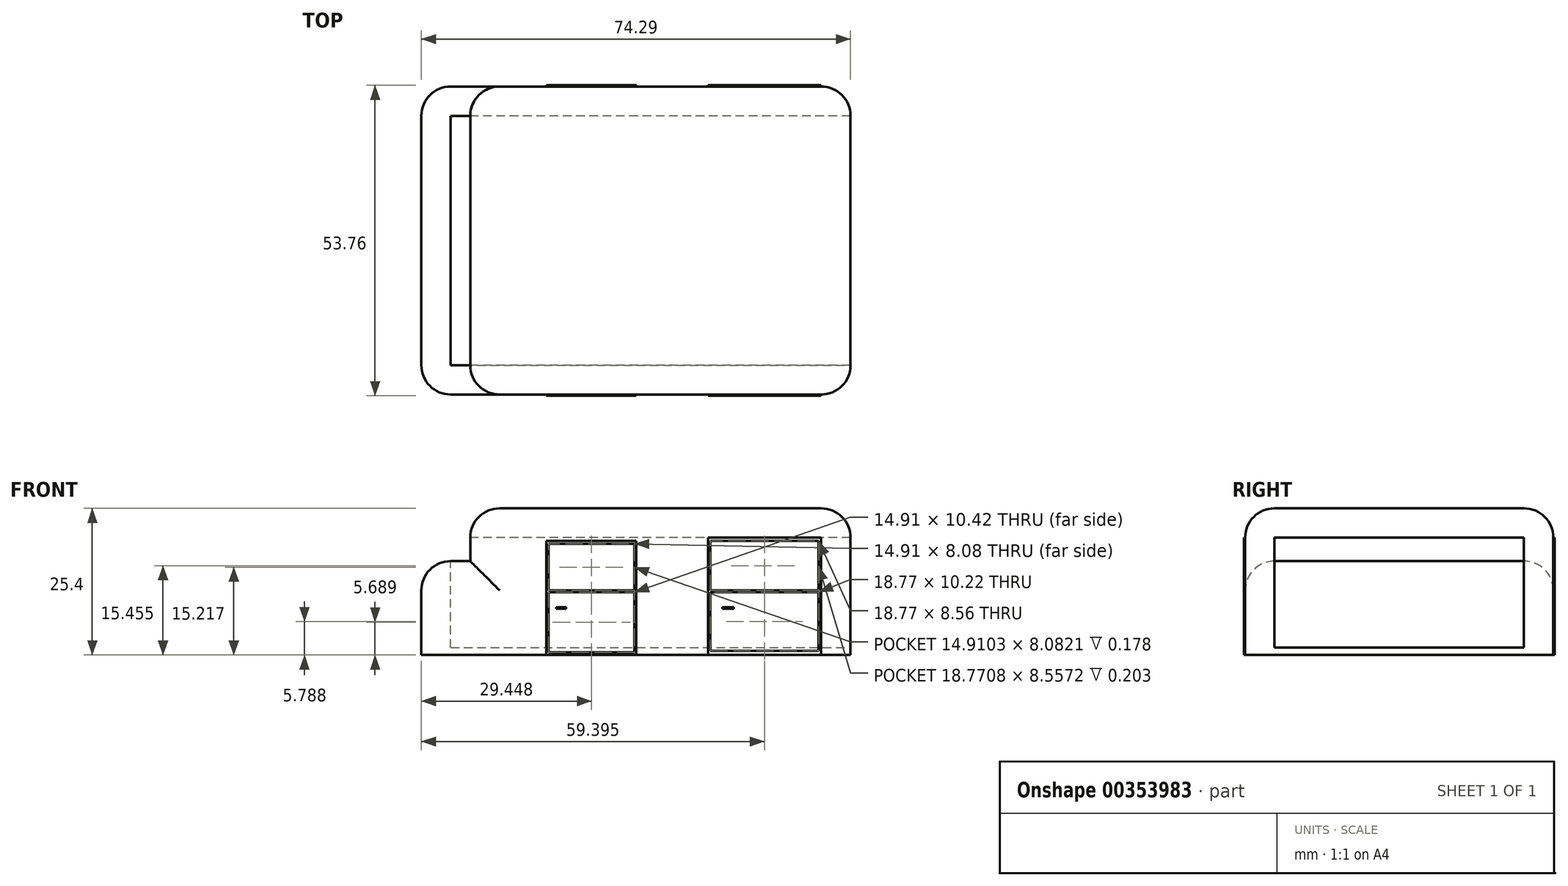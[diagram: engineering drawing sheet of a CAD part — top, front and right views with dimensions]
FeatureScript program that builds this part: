
annotation { "Feature Type Name" : "Feature", "Feature Type Description" : "" }
export const myFeature = defineFeature(function(context is Context, id is Id, definition is map)
    precondition{}
    {
        {
            var Q0;
            Q0=qCreatedBy(makeId("Top.planeOp"),FACE);
            var sketch = newSketch(context, id + "F0", { "sketchPlane" : qUnion([Q0])});
            skLineSegment(sketch, "E0.bottom", {"start": v(32.91, -26.68) * mm, "end": v(-32.91, -26.68) * mm});
            skLineSegment(sketch, "E0.top", {"start": v(32.91, 26.68) * mm, "end": v(-32.91, 26.68) * mm});
            skLineSegment(sketch, "E0.left", {"start": v(32.91, -26.68) * mm, "end": v(32.91, 26.68) * mm});
            skLineSegment(sketch, "E0.right", {"start": v(-32.91, -26.68) * mm, "end": v(-32.91, 26.68) * mm});
            skPoint(sketch, "E0.middle", {"position": v(0, 0) * mm});
            skLineSegment(sketch, "E1", {"start": v(-32.91, 26.68) * mm, "end": v(-41.38, 26.68) * mm});
            skLineSegment(sketch, "E2", {"start": v(-41.38, 26.68) * mm, "end": v(-41.38, -26.68) * mm});
            skLineSegment(sketch, "E3", {"start": v(-41.38, -26.68) * mm, "end": v(-32.91, -26.68) * mm});
            skSolve(sketch);
        }
        {
            var Q0;
            {var subQ3=sQuery(id+"F0.wireOp",EDGE,"E0.bottom");Q0=makeQuery(id+"F0.imprint","IMPRINT",FACE,{"disambiguationData":[TD([[makeQuery(id+"F0.imprint","IMPRINT",EDGE,{"derivedFrom":subQ3}),-1.0]])]});}
            extrude(context, id + "F1", {"entities" : qUnion([Q0]), "depth" : 25.4 * mm});
        }
        {
            var Q0;
            Q0=makeQuery(id+"F0.imprint","IMPRINT",FACE,{"disambiguationData":[TD([[makeQuery(id+"F0.imprint","IMPRINT",EDGE,{"derivedFrom":sQuery(id+"F0.wireOp",EDGE,"E0.right")}),1.0]])]});
            extrude(context, id + "F2", {"entities" : qUnion([Q0]), "operationType" : NewBodyOperationType.ADD, "depth" : 16.26 * mm});
        }
        {
            var Q0;
            Q0=makeQuery(id+"F1.opExtrude","CAP_EDGE",EDGE,{"disambiguationData":[OSD([sQuery(id+"F0.wireOp",EDGE,"E0.right")])],"isStart":false});
            var Q1;
            Q1=makeQuery(id+"F2.opExtrude","CAP_EDGE",EDGE,{"disambiguationData":[OSD([sQuery(id+"F0.wireOp",EDGE,"E2")])],"isStart":false});
            fillet(context, id + "F3", {"entities" : qUnion([Q0, Q1]), "radius" : 5.08 * mm, "tangentPropagation" : true, "allowEdgeOverflow" : false});
        }
        {
            var Q0;
            Q0=makeQuery(id+"F1.opExtrude","CAP_EDGE",EDGE,{"disambiguationData":[OSD([sQuery(id+"F0.wireOp",EDGE,"E0.bottom")])],"isStart":false});
            var Q1;
            Q1=makeQuery(id+"F1.opExtrude","CAP_EDGE",EDGE,{"disambiguationData":[OSD([sQuery(id+"F0.wireOp",EDGE,"E0.top")])],"isStart":false});
            var Q2;
            Q2=makeQuery(id+"F1.opExtrude","CAP_EDGE",EDGE,{"disambiguationData":[OSD([sQuery(id+"F0.wireOp",EDGE,"E0.left")])],"isStart":false});
            var Q3;
            Q3=makeQuery(id+"FWzkn3ZvCIPQpPH_1.opExtrude","CAP_EDGE",EDGE,{"disambiguationData":[OSD([sQuery(id+"F0.wireOp",EDGE,"xIUMnqJd-k26k-LNKP-rsLH-VAkoYsiP5ywj")])],"isStart":false});
            var Q4;
            Q4=makeQuery(id+"FWzkn3ZvCIPQpPH_1.opExtrude","CAP_EDGE",EDGE,{"disambiguationData":[OSD([sQuery(id+"F0.wireOp",EDGE,"11fe9602-79eb-4884-af82-4b5a2583d0040.MirrorCS")])],"isStart":false});
            var Q5;
            Q5=makeQuery(id+"FWzkn3ZvCIPQpPH_1.opExtrude","CAP_EDGE",EDGE,{"disambiguationData":[OSD([sQuery(id+"F0.wireOp",EDGE,"2cLvPiks-i8wb-QU2D-KdXj-OwnOsGgTFJpn")])],"isStart":false});
            var Q6;
            Q6=makeQuery(id+"F3.opFillet","BLEND_EDGE",EDGE,{"blendedFrom":[makeQuery(id+"F2.opExtrude","CAP_EDGE",EDGE,{"disambiguationData":[OSD([sQuery(id+"F0.wireOp",EDGE,"E2")])],"isStart":false}),makeQuery(id+"F2.boolean.opBoolean","MERGE",FACE,{"derivedFrom":[makeQuery(id+"F1.opExtrude","SWEPT_FACE",FACE,{"disambiguationData":[OSD([sQuery(id+"F0.wireOp",EDGE,"E0.bottom")])]}),makeQuery(id+"F2.opExtrude","SWEPT_FACE",FACE,{"disambiguationData":[OSD([sQuery(id+"F0.wireOp",EDGE,"E3")])]})]})],"blendedInto":[makeQuery(id+"F2.boolean.opBoolean","MERGE",FACE,{"derivedFrom":[makeQuery(id+"F1.opExtrude","SWEPT_FACE",FACE,{"disambiguationData":[OSD([sQuery(id+"F0.wireOp",EDGE,"E0.bottom")])]}),makeQuery(id+"F2.opExtrude","SWEPT_FACE",FACE,{"disambiguationData":[OSD([sQuery(id+"F0.wireOp",EDGE,"E3")])]})]})]});
            var Q7;
            Q7=makeQuery(id+"F3.opFillet","BLEND_EDGE",EDGE,{"blendedFrom":[makeQuery(id+"F2.opExtrude","CAP_EDGE",EDGE,{"disambiguationData":[OSD([sQuery(id+"F0.wireOp",EDGE,"E2")])],"isStart":false}),makeQuery(id+"F2.boolean.opBoolean","MERGE",FACE,{"derivedFrom":[makeQuery(id+"F1.opExtrude","SWEPT_FACE",FACE,{"disambiguationData":[OSD([sQuery(id+"F0.wireOp",EDGE,"E0.top")])]}),makeQuery(id+"F2.opExtrude","SWEPT_FACE",FACE,{"disambiguationData":[OSD([sQuery(id+"F0.wireOp",EDGE,"E1")])]})]})],"blendedInto":[makeQuery(id+"F2.boolean.opBoolean","MERGE",FACE,{"derivedFrom":[makeQuery(id+"F1.opExtrude","SWEPT_FACE",FACE,{"disambiguationData":[OSD([sQuery(id+"F0.wireOp",EDGE,"E0.top")])]}),makeQuery(id+"F2.opExtrude","SWEPT_FACE",FACE,{"disambiguationData":[OSD([sQuery(id+"F0.wireOp",EDGE,"E1")])]})]})]});
            fillet(context, id + "F4", {"entities" : qUnion([Q0, Q1, Q2, Q3, Q4, Q5, Q6, Q7]), "radius" : 5.08 * mm, "tangentPropagation" : true, "allowEdgeOverflow" : false});
        }
        {
            var Q0;
            Q0=makeQuery(id+"FOH9foroh4Kcc7F_1.opExtrude","CAP_EDGE",EDGE,{"disambiguationData":[OSD([sQuery(id+"F0.wireOp",EDGE,"680b5d57-0d46-4cfd-9d55-bcc36bf5c1430.MirrorCS")])],"isStart":false});
            var Q1;
            Q1=makeQuery(id+"FOH9foroh4Kcc7F_1.opExtrude","CAP_EDGE",EDGE,{"disambiguationData":[OSD([sQuery(id+"F0.wireOp",EDGE,"xIUMnqJd-k26k-LNKP-rsLH-VAkoYsiP5ywj"),sQuery(id+"F0.wireOp",EDGE,"v0cE8wne-bUnx-vWfc-z6Zt-nEohdFppC2Xa"),sQuery(id+"F0.wireOp",EDGE,"guTs02fZ-XOxl-c3qa-s84M-HNOjAy1qtpT4")])],"isStart":false});
            var Q2;
            Q2=makeQuery(id+"FOH9foroh4Kcc7F_1.opExtrude","CAP_EDGE",EDGE,{"disambiguationData":[OSD([sQuery(id+"F0.wireOp",EDGE,"3jDZVk8o-DRke-lTU3-k8Uu-l1xdUuneoS6k")])],"isStart":false});
            var Q3;
            Q3=makeQuery(id+"F1.opExtrude","SWEPT_EDGE",EDGE,{"disambiguationData":[OSD([sQuery(id+"F0.wireOp",EDGE,"E0.bottom"),sQuery(id+"F0.wireOp",EDGE,"E0.left"),sQuery(id+"F0.wireOp",EDGE,"680b5d57-0d46-4cfd-9d55-bcc36bf5c1430.MirrorCS")])]});
            var Q4;
            Q4=makeQuery(id+"F1.opExtrude","SWEPT_EDGE",EDGE,{"disambiguationData":[OSD([sQuery(id+"F0.wireOp",EDGE,"E0.top"),sQuery(id+"F0.wireOp",EDGE,"E0.left"),sQuery(id+"F0.wireOp",EDGE,"3jDZVk8o-DRke-lTU3-k8Uu-l1xdUuneoS6k")])]});
            fillet(context, id + "F5", {"entities" : qUnion([Q0, Q1, Q2, Q3, Q4]), "radius" : 5.08 * mm, "tangentPropagation" : true, "allowEdgeOverflow" : false});
        }
        {
            var Q0;
            Q0=makeQuery(id+"F2.boolean.opBoolean","MERGE",FACE,{"derivedFrom":[makeQuery(id+"F1.opExtrude","SWEPT_FACE",FACE,{"disambiguationData":[OSD([sQuery(id+"F0.wireOp",EDGE,"E0.bottom")])]}),makeQuery(id+"F2.opExtrude","SWEPT_FACE",FACE,{"disambiguationData":[OSD([sQuery(id+"F0.wireOp",EDGE,"E3")])]})]});
            var sketch = newSketch(context, id + "F6", { "sketchPlane" : qUnion([Q0])});
            skLineSegment(sketch, "E4.MirrorCS", {"start": v(27.4, 11.18) * mm, "end": v(8.63, 11.18) * mm});
            skLineSegment(sketch, "E5.MirrorCS", {"start": v(8.23, 11.18) * mm, "end": v(8.23, 20.32) * mm});
            skLineSegment(sketch, "E6.MirrorCS", {"start": v(8.23, 11.18) * mm, "end": v(8.23, 0) * mm});
            skLineSegment(sketch, "E7.MirrorCS", {"start": v(12.7, 8.28) * mm, "end": v(10.72, 8.28) * mm});
            skLineSegment(sketch, "E8.MirrorCS", {"start": v(27.83, 11.18) * mm, "end": v(27.83, 0) * mm});
            skLineSegment(sketch, "E9.MirrorCS", {"start": v(8.23, 0) * mm, "end": v(27.83, 0) * mm});
            skLineSegment(sketch, "E10", {"start": v(-27.83, 11.18) * mm, "end": v(-19.78, 11.18) * mm});
            skLineSegment(sketch, "E11", {"start": v(-19.78, 11.18) * mm, "end": v(-19.78, 19.73) * mm});
            skLineSegment(sketch, "E12", {"start": v(-4.17, 11.18) * mm, "end": v(-4.17, 0) * mm});
            skLineSegment(sketch, "E13", {"start": v(-4.17, 0) * mm, "end": v(-19.78, 0) * mm});
            skLineSegment(sketch, "E14", {"start": v(-19.78, 0) * mm, "end": v(-19.78, 11.18) * mm});
            skLineSegment(sketch, "E15", {"start": v(-4.48, 11.18) * mm, "end": v(-19.39, 11.18) * mm});
            skLineSegment(sketch, "E16", {"start": v(-4.17, 11.18) * mm, "end": v(-4.17, 19.73) * mm});
            skLineSegment(sketch, "E17", {"start": v(-19.78, 19.73) * mm, "end": v(-4.17, 19.73) * mm});
            skLineSegment(sketch, "E18", {"start": v(8.63, 19.73) * mm, "end": v(27.4, 19.73) * mm});
            skLineSegment(sketch, "E19", {"start": v(27.83, 19.73) * mm, "end": v(27.83, 11.18) * mm});
            skLineSegment(sketch, "E20", {"start": v(27.83, 19.73) * mm, "end": v(27.83, 20.32) * mm});
            skLineSegment(sketch, "E21", {"start": v(27.83, 20.32) * mm, "end": v(8.23, 20.32) * mm});
            skLineSegment(sketch, "E22", {"start": v(-18.03, 8.28) * mm, "end": v(-16.3, 8.28) * mm});
            skLineSegment(sketch, "E23", {"start": v(-18.03, 8.28) * mm, "end": v(-18.03, 8) * mm});
            skLineSegment(sketch, "E24", {"start": v(-18.03, 8) * mm, "end": v(-16.3, 8) * mm});
            skLineSegment(sketch, "E25", {"start": v(-16.3, 8) * mm, "end": v(-16.3, 8.28) * mm});
            skLineSegment(sketch, "E26", {"start": v(10.72, 8.28) * mm, "end": v(10.72, 8) * mm});
            skLineSegment(sketch, "E27", {"start": v(10.72, 8) * mm, "end": v(12.7, 8) * mm});
            skLineSegment(sketch, "E28", {"start": v(12.7, 8) * mm, "end": v(12.7, 8.28) * mm});
            skLineSegment(sketch, "E29", {"start": v(-19.39, 10.9) * mm, "end": v(-4.48, 10.9) * mm});
            skLineSegment(sketch, "E30", {"start": v(-4.48, 11.18) * mm, "end": v(-4.48, 19.26) * mm});
            skLineSegment(sketch, "E31", {"start": v(-19.39, 11.18) * mm, "end": v(-19.39, 19.26) * mm});
            skLineSegment(sketch, "E32", {"start": v(-19.39, 19.26) * mm, "end": v(-4.48, 19.26) * mm});
            skLineSegment(sketch, "E33", {"start": v(-19.39, 10.9) * mm, "end": v(-19.39, 0.48) * mm});
            skLineSegment(sketch, "E34", {"start": v(-4.48, 10.9) * mm, "end": v(-4.48, 0.48) * mm});
            skLineSegment(sketch, "E35", {"start": v(-19.39, 0.48) * mm, "end": v(-4.48, 0.48) * mm});
            skPoint(sketch, "E36.orphan", {"position": v(-4.17, 10.9) * mm});
            skLineSegment(sketch, "E37", {"start": v(8.63, 19.73) * mm, "end": v(8.63, 11.18) * mm});
            skLineSegment(sketch, "E38", {"start": v(8.63, 10.9) * mm, "end": v(27.4, 10.9) * mm});
            skLineSegment(sketch, "E39", {"start": v(27.4, 19.73) * mm, "end": v(27.4, 11.18) * mm});
            skLineSegment(sketch, "E40", {"start": v(8.63, 10.9) * mm, "end": v(8.63, 0.68) * mm});
            skLineSegment(sketch, "E41", {"start": v(8.63, 0.68) * mm, "end": v(27.4, 0.68) * mm});
            skLineSegment(sketch, "E42", {"start": v(27.4, 10.9) * mm, "end": v(27.4, 0.68) * mm});
            skPoint(sketch, "E43.orphan", {"position": v(8.23, 11.18) * mm});
            skPoint(sketch, "E44.orphan", {"position": v(8.23, 10.9) * mm});
            skPoint(sketch, "E45.orphan", {"position": v(8.23, 19.73) * mm});
            skSolve(sketch);
        }
        {
            var Q0;
            Q0=makeQuery(id+"F1.opExtrude","SWEPT_FACE",FACE,{"disambiguationData":[OSD([sQuery(id+"F0.wireOp",EDGE,"E0.right")])]});
            var sketch = newSketch(context, id + "F7", { "sketchPlane" : qUnion([Q0])});
            skLineSegment(sketch, "E46", {"start": v(-21.6, 20.32) * mm, "end": v(-21.6, 16.26) * mm});
            skLineSegment(sketch, "E47", {"start": v(-21.6, 16.26) * mm, "end": v(21.6, 16.26) * mm});
            skLineSegment(sketch, "E48", {"start": v(21.6, 16.26) * mm, "end": v(21.6, 20.32) * mm});
            skLineSegment(sketch, "E49", {"start": v(21.6, 20.32) * mm, "end": v(-21.6, 20.32) * mm});
            skSolve(sketch);
        }
        {
            var Q0;
            Q0=makeQuery(id+"F6.imprint","IMPRINT",FACE,{"disambiguationData":[TD([[makeQuery(id+"F6.imprint","IMPRINT",EDGE,{"derivedFrom":sQuery(id+"F6.wireOp",EDGE,"E11")}),-1.0]])]});
            var Q1;
            Q1=makeQuery(id+"F6.imprint","IMPRINT",FACE,{"disambiguationData":[TD([[makeQuery(id+"F6.imprint","IMPRINT",EDGE,{"derivedFrom":sQuery(id+"F6.wireOp",EDGE,"E22")}),-1.0]])]});
            extrude(context, id + "F8", {"entities" : qUnion([Q0, Q1]), "operationType" : NewBodyOperationType.ADD, "depth" : 0.18 * mm});
        }
        {
            var Q0;
            Q0=makeQuery(id+"F6.imprint","IMPRINT",FACE,{"disambiguationData":[TD([[makeQuery(id+"F6.imprint","IMPRINT",EDGE,{"derivedFrom":sQuery(id+"F6.wireOp",EDGE,"E4.MirrorCS")}),1.0]])]});
            var Q1;
            Q1=makeQuery(id+"F6.imprint","IMPRINT",FACE,{"disambiguationData":[TD([[makeQuery(id+"F6.imprint","IMPRINT",EDGE,{"derivedFrom":sQuery(id+"F6.wireOp",EDGE,"E7.MirrorCS")}),1.0]])]});
            extrude(context, id + "F9", {"entities" : qUnion([Q0, Q1]), "operationType" : NewBodyOperationType.ADD, "depth" : 0.2 * mm});
        }
        {
            var Q0;
            Q0=makeQuery(id+"F2.boolean.opBoolean","MERGE",FACE,{"derivedFrom":[makeQuery(id+"F1.opExtrude","SWEPT_FACE",FACE,{"disambiguationData":[OSD([sQuery(id+"F0.wireOp",EDGE,"E0.top")])]}),makeQuery(id+"F2.opExtrude","SWEPT_FACE",FACE,{"disambiguationData":[OSD([sQuery(id+"F0.wireOp",EDGE,"E1")])]})]});
            var sketch = newSketch(context, id + "F10", { "sketchPlane" : qUnion([Q0])});
            skLineSegment(sketch, "E50", {"start": v(-27.42, 0.7) * mm, "end": v(-27.42, 10.9) * mm});
            skLineSegment(sketch, "E51", {"start": v(-27.42, 10.9) * mm, "end": v(-8.63, 10.9) * mm});
            skLineSegment(sketch, "E52", {"start": v(-8.63, 10.9) * mm, "end": v(-8.63, 0.69) * mm});
            skLineSegment(sketch, "E53", {"start": v(-8.63, 0.69) * mm, "end": v(-27.42, 0.7) * mm});
            skLineSegment(sketch, "E54", {"start": v(-8.23, 0) * mm, "end": v(-8.23, 10.9) * mm});
            skLineSegment(sketch, "E55", {"start": v(-8.23, 10.9) * mm, "end": v(-8.23, 20.32) * mm});
            skLineSegment(sketch, "E56", {"start": v(-8.23, 20.32) * mm, "end": v(-27.83, 20.32) * mm});
            skLineSegment(sketch, "E57", {"start": v(-27.83, 20.32) * mm, "end": v(-27.83, 11.29) * mm});
            skLineSegment(sketch, "E58", {"start": v(-27.83, 11.29) * mm, "end": v(-27.83, 10.9) * mm});
            skLineSegment(sketch, "E59", {"start": v(-27.83, 10.9) * mm, "end": v(-27.83, 0) * mm});
            skLineSegment(sketch, "E60", {"start": v(-27.83, 0) * mm, "end": v(-8.23, 0) * mm});
            skLineSegment(sketch, "E61", {"start": v(-27.4, 19.74) * mm, "end": v(-8.63, 19.74) * mm});
            skLineSegment(sketch, "E62", {"start": v(-12.7, 8.29) * mm, "end": v(-12.7, 8) * mm});
            skLineSegment(sketch, "E63", {"start": v(-12.7, 8) * mm, "end": v(-10.72, 8) * mm});
            skLineSegment(sketch, "E64", {"start": v(-10.72, 8) * mm, "end": v(-10.72, 8.28) * mm});
            skLineSegment(sketch, "E65", {"start": v(-10.72, 8.28) * mm, "end": v(-12.7, 8.29) * mm});
            skLineSegment(sketch, "E66", {"start": v(-27.4, 11.18) * mm, "end": v(-27.4, 19.74) * mm});
            skLineSegment(sketch, "E67", {"start": v(-8.63, 11.17) * mm, "end": v(-8.63, 19.74) * mm});
            skLineSegment(sketch, "E68", {"start": v(-8.63, 11.17) * mm, "end": v(-27.4, 11.18) * mm});
            skLineSegment(sketch, "E69", {"start": v(16.3, 8.28) * mm, "end": v(18.03, 8.28) * mm});
            skLineSegment(sketch, "E70", {"start": v(18.03, 8.28) * mm, "end": v(18.03, 8) * mm});
            skLineSegment(sketch, "E71", {"start": v(18.03, 8) * mm, "end": v(16.3, 8) * mm});
            skLineSegment(sketch, "E72", {"start": v(16.3, 8) * mm, "end": v(16.3, 8.28) * mm});
            skLineSegment(sketch, "E73", {"start": v(4.47, 10.91) * mm, "end": v(4.47, 0.48) * mm});
            skLineSegment(sketch, "E74", {"start": v(4.47, 0.48) * mm, "end": v(19.39, 0.48) * mm});
            skLineSegment(sketch, "E75", {"start": v(19.39, 0.48) * mm, "end": v(19.39, 10.88) * mm});
            skLineSegment(sketch, "E76", {"start": v(19.39, 10.88) * mm, "end": v(4.47, 10.91) * mm});
            skLineSegment(sketch, "E77", {"start": v(4.17, 10.91) * mm, "end": v(4.17, 0) * mm});
            skLineSegment(sketch, "E78", {"start": v(4.17, 0) * mm, "end": v(19.77, 0) * mm});
            skLineSegment(sketch, "E79", {"start": v(19.77, 0) * mm, "end": v(19.77, 10.91) * mm});
            skLineSegment(sketch, "E80", {"start": v(19.77, 11.2) * mm, "end": v(27.83, 11.18) * mm});
            skLineSegment(sketch, "E81", {"start": v(19.39, 11.2) * mm, "end": v(19.39, 19.25) * mm});
            skLineSegment(sketch, "E82", {"start": v(19.39, 19.25) * mm, "end": v(4.45, 19.25) * mm});
            skLineSegment(sketch, "E83", {"start": v(4.45, 19.25) * mm, "end": v(4.47, 11.2) * mm});
            skLineSegment(sketch, "E84", {"start": v(4.47, 11.2) * mm, "end": v(19.39, 11.2) * mm});
            skLineSegment(sketch, "E85", {"start": v(19.77, 19.75) * mm, "end": v(4.15, 19.75) * mm});
            skLineSegment(sketch, "E86", {"start": v(4.15, 19.75) * mm, "end": v(4.15, 11.2) * mm});
            skLineSegment(sketch, "E87", {"start": v(4.15, 11.2) * mm, "end": v(4.17, 10.91) * mm});
            skLineSegment(sketch, "E88", {"start": v(19.77, 19.75) * mm, "end": v(19.77, 11.2) * mm});
            skLineSegment(sketch, "E89", {"start": v(19.77, 10.91) * mm, "end": v(19.77, 11.2) * mm});
            skSolve(sketch);
        }
        {
            var Q0;
            Q0=makeQuery(id+"F10.imprint","IMPRINT",FACE,{"disambiguationData":[TD([[makeQuery(id+"F10.imprint","IMPRINT",EDGE,{"derivedFrom":sQuery(id+"F10.wireOp",EDGE,"E50")}),1.0]])]});
            var Q1;
            Q1=makeQuery(id+"F10.imprint","IMPRINT",FACE,{"disambiguationData":[TD([[makeQuery(id+"F10.imprint","IMPRINT",EDGE,{"derivedFrom":sQuery(id+"F10.wireOp",EDGE,"E62")}),1.0]])]});
            var Q2;
            Q2=makeQuery(id+"F10.imprint","IMPRINT",FACE,{"disambiguationData":[TD([[makeQuery(id+"F10.imprint","IMPRINT",EDGE,{"derivedFrom":sQuery(id+"F10.wireOp",EDGE,"E73")}),-1.0]])]});
            var Q3;
            Q3=makeQuery(id+"F10.imprint","IMPRINT",FACE,{"disambiguationData":[TD([[makeQuery(id+"F10.imprint","IMPRINT",EDGE,{"derivedFrom":sQuery(id+"F10.wireOp",EDGE,"E69")}),-1.0]])]});
            extrude(context, id + "F11", {"entities" : qUnion([Q0, Q1, Q2, Q3]), "operationType" : NewBodyOperationType.ADD, "depth" : 0.2 * mm});
        }
        {
            var Q0;
            Q0=makeQuery(id+"F7.imprint","IMPRINT",FACE,{"disambiguationData":[TD([[makeQuery(id+"F7.imprint","IMPRINT",EDGE,{"derivedFrom":sQuery(id+"F7.wireOp",EDGE,"E46")}),1.0]])]});
            extrude(context, id + "F12", {"entities" : qUnion([Q0]), "operationType" : NewBodyOperationType.REMOVE, "oppositeDirection" : true, "depth" : 66.04 * mm});
        }
        {
            var Q0;
            Q0=makeQuery(id+"F12.boolean.opBoolean","MERGE",FACE,{"derivedFrom":[makeQuery(id+"F2.opExtrude","CAP_FACE",FACE,{"disambiguationData":[OSD([sQuery(id+"F0.wireOp",EDGE,"E0.right"),sQuery(id+"F0.wireOp",EDGE,"E1"),sQuery(id+"F0.wireOp",EDGE,"E2"),sQuery(id+"F0.wireOp",EDGE,"E3")])],"isStart":false}),makeQuery(id+"F12.opExtrude","SWEPT_FACE",FACE,{"disambiguationData":[OSD([sQuery(id+"F7.wireOp",EDGE,"E47")])]})]});
            extrude(context, id + "F13", {"entities" : qUnion([Q0]), "operationType" : NewBodyOperationType.REMOVE, "oppositeDirection" : true, "depth" : 15 * mm});
        }
    });
